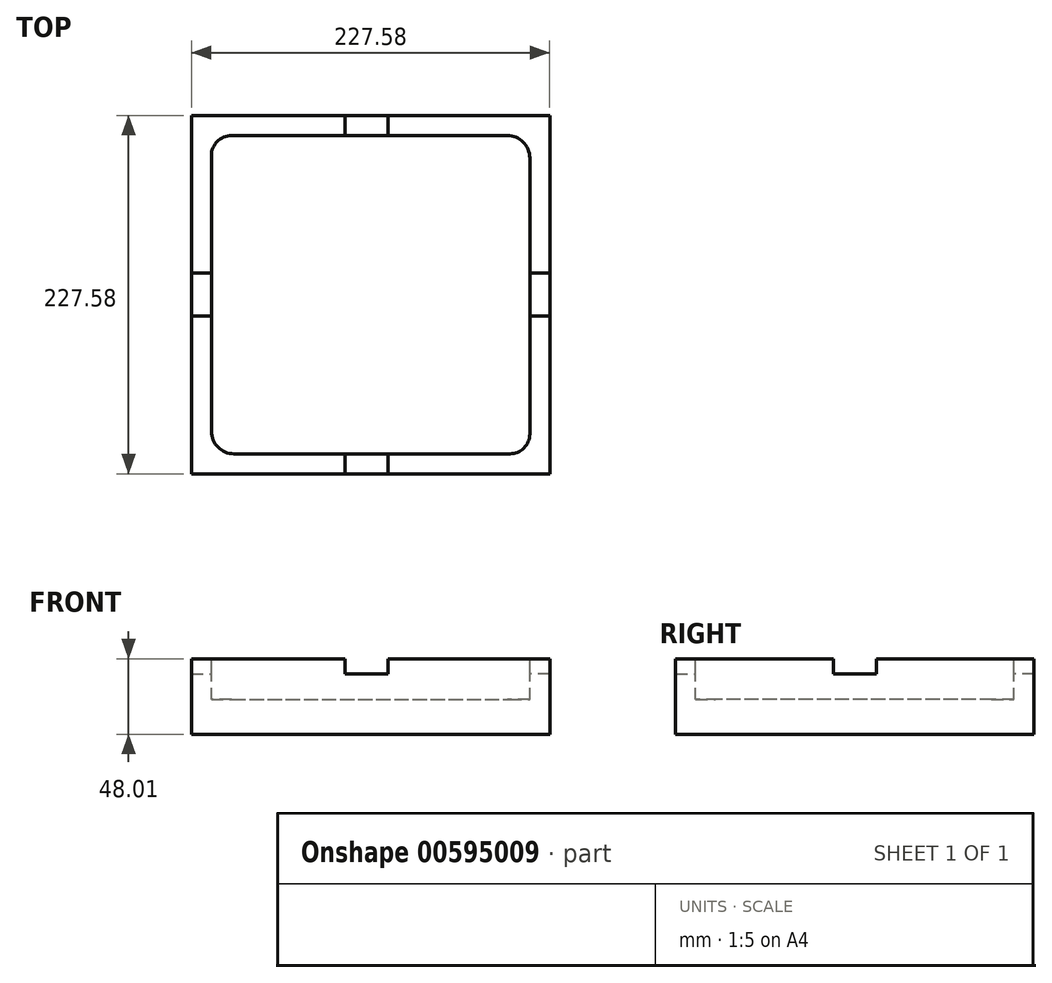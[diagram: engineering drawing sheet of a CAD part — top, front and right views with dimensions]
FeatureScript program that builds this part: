
annotation { "Feature Type Name" : "Feature", "Feature Type Description" : "" }
export const myFeature = defineFeature(function(context is Context, id is Id, definition is map)
    precondition{}
    {
        {
            var Q0;
            Q0=qCreatedBy(makeId("Top.planeOp"),FACE);
            var sketch = newSketch(context, id + "F0", { "sketchPlane" : qUnion([Q0])});
            skLineSegment(sketch, "E0.bottom", {"start": v(113.8, 113.8) * mm, "end": v(-113.8, 113.8) * mm});
            skLineSegment(sketch, "E0.top", {"start": v(113.8, -113.8) * mm, "end": v(-113.8, -113.8) * mm});
            skLineSegment(sketch, "E0.left", {"start": v(113.8, 113.8) * mm, "end": v(113.8, -113.8) * mm});
            skLineSegment(sketch, "E0.right", {"start": v(-113.8, 113.8) * mm, "end": v(-113.8, -113.8) * mm});
            skPoint(sketch, "E0.middle", {"position": v(0, 0) * mm});
            skLineSegment(sketch, "E1", {"start": v(0, -188.89) * mm, "end": v(0, 205.95) * mm, "construction": true});
            skPoint(sketch, "E1.startSnap0", {"position": v(0, -113.8) * mm});
            skPoint(sketch, "E1.endSnap0", {"position": v(0, 113.8) * mm});
            skLineSegment(sketch, "E2", {"start": v(-219.67, 0) * mm, "end": v(231.95, 0) * mm, "construction": true});
            skPoint(sketch, "E2.endSnap0", {"position": v(113.8, 0) * mm});
            skSolve(sketch);
        }
        {
            var Q0;
            Q0 = qSketchRegion(id + "F0", true);
            extrude(context, id + "F1", {"entities" : qUnion([Q0]), "depth" : 48 * mm, "offsetDistance" : 25.4 * mm});
        }
        {
            var Q0;
            Q0=makeQuery(id+"F1.opExtrude","CAP_FACE",FACE,{"disambiguationData":[OSD([sQuery(id+"F0.wireOp",EDGE,"E0.bottom"),sQuery(id+"F0.wireOp",EDGE,"E0.top"),sQuery(id+"F0.wireOp",EDGE,"E0.left"),sQuery(id+"F0.wireOp",EDGE,"E0.right")])],"isStart":false});
            var sketch = newSketch(context, id + "F2", { "sketchPlane" : qUnion([Q0])});
            skLineSegment(sketch, "E3", {"start": v(-88.4, 101.1) * mm, "end": v(86.8, 101.1) * mm});
            skLineSegment(sketch, "E4", {"start": v(-101.1, 88.4) * mm, "end": v(-101.1, -86.8) * mm});
            skLineSegment(sketch, "E5", {"start": v(0, -144.22) * mm, "end": v(0, 136.7) * mm, "construction": true});
            skLineSegment(sketch, "E6", {"start": v(188.13, 0) * mm, "end": v(-233, 0) * mm, "construction": true});
            skPoint(sketch, "E6.startSnap0", {"position": v(113.8, 0) * mm});
            skLineSegment(sketch, "E7.MirrorCS", {"start": v(-86.8, -101.1) * mm, "end": v(88.4, -101.1) * mm});
            skLineSegment(sketch, "E8.MirrorCS", {"start": v(101.1, 86.8) * mm, "end": v(101.1, -88.4) * mm});
            skArc(sketch, "E9.filletArc", {"start": v(-88.4, 101.1) * mm, "mid": v(-97.37, 97.37) * mm, "end": v(-101.1, 88.4) * mm});
            skPoint(sketch, "E10.visualSharp", {"position": v(101.1, -101.1) * mm});
            skArc(sketch, "E10.filletArc", {"start": v(88.4, -101.1) * mm, "mid": v(97.37, -97.37) * mm, "end": v(101.1, -88.4) * mm});
            skPoint(sketch, "E11.visualSharp", {"position": v(101.1, 101.1) * mm});
            skArc(sketch, "E11.filletArc", {"start": v(101.1, 86.8) * mm, "mid": v(96.9, 96.9) * mm, "end": v(86.8, 101.1) * mm});
            skPoint(sketch, "E12.visualSharp", {"position": v(-101.1, -101.1) * mm});
            skArc(sketch, "E12.filletArc", {"start": v(-101.1, -86.8) * mm, "mid": v(-96.9, -96.9) * mm, "end": v(-86.8, -101.1) * mm});
            skLineSegment(sketch, "E13", {"start": v(13.91, 101.1) * mm, "end": v(13.91, 113.8) * mm, "construction": true});
            skLineSegment(sketch, "E14", {"start": v(101.1, -11.17) * mm, "end": v(113.8, -11.17) * mm, "construction": true});
            skSolve(sketch);
        }
        {
            var Q0;
            Q0=makeQuery(id+"F2.imprint","IMPRINT",FACE,{"disambiguationData":[TD([[makeQuery(id+"F2.imprint","IMPRINT",EDGE,{"derivedFrom":sQuery(id+"F2.wireOp",EDGE,"E3")}),-1.0]])]});
            extrude(context, id + "F3", {"entities" : qUnion([Q0]), "operationType" : NewBodyOperationType.REMOVE, "oppositeDirection" : true, "depth" : 25.9 * mm, "offsetDistance" : 25.4 * mm});
        }
        {
            var Q0;
            Q0=makeQuery(id+"F1.opExtrude","CAP_FACE",FACE,{"disambiguationData":[OSD([sQuery(id+"F0.wireOp",EDGE,"E0.bottom"),sQuery(id+"F0.wireOp",EDGE,"E0.top"),sQuery(id+"F0.wireOp",EDGE,"E0.left"),sQuery(id+"F0.wireOp",EDGE,"E0.right")])],"isStart":false});
            var sketch = newSketch(context, id + "F4", { "sketchPlane" : qUnion([Q0])});
            skLineSegment(sketch, "E15", {"start": v(0, 153.68) * mm, "end": v(0, -179.49) * mm, "construction": true});
            skLineSegment(sketch, "E16", {"start": v(-246.34, 0) * mm, "end": v(288.7, 0) * mm, "construction": true});
            skLineSegment(sketch, "E17.bottom", {"start": v(11.1, 113.8) * mm, "end": v(-16.33, 113.8) * mm});
            skLineSegment(sketch, "E17.top", {"start": v(11.1, 101.1) * mm, "end": v(-16.33, 101.1) * mm});
            skLineSegment(sketch, "E17.left", {"start": v(11.1, 113.8) * mm, "end": v(11.1, 101.1) * mm});
            skLineSegment(sketch, "E17.right", {"start": v(-16.33, 113.8) * mm, "end": v(-16.33, 101.1) * mm});
            skPoint(sketch, "E17.middle", {"position": v(-2.61, 107.44) * mm});
            skLineSegment(sketch, "E18", {"start": v(113.8, 0) * mm, "end": v(101.1, 0) * mm});
            skLineSegment(sketch, "E19.bottom", {"start": v(113.8, 13.72) * mm, "end": v(101.1, 13.72) * mm});
            skLineSegment(sketch, "E19.top", {"start": v(113.8, -13.72) * mm, "end": v(101.1, -13.72) * mm});
            skLineSegment(sketch, "E19.left", {"start": v(113.8, 13.72) * mm, "end": v(113.8, -13.72) * mm});
            skLineSegment(sketch, "E19.right", {"start": v(101.1, 13.72) * mm, "end": v(101.1, -13.72) * mm});
            skPoint(sketch, "E19.middle", {"position": v(107.44, 0) * mm});
            skLineSegment(sketch, "E20.MirrorCS", {"start": v(11.1, -101.1) * mm, "end": v(-16.33, -101.1) * mm});
            skLineSegment(sketch, "E21.MirrorCS", {"start": v(11.1, -113.8) * mm, "end": v(-16.33, -113.8) * mm});
            skLineSegment(sketch, "E22.MirrorCS", {"start": v(11.1, -113.8) * mm, "end": v(11.1, -101.1) * mm});
            skLineSegment(sketch, "E23.MirrorCS", {"start": v(-16.33, -113.8) * mm, "end": v(-16.33, -101.1) * mm});
            skLineSegment(sketch, "E24.MirrorCS", {"start": v(-113.8, 13.72) * mm, "end": v(-101.1, 13.72) * mm});
            skLineSegment(sketch, "E25.MirrorCS", {"start": v(-101.1, 13.72) * mm, "end": v(-101.1, -13.72) * mm});
            skLineSegment(sketch, "E26.MirrorCS", {"start": v(-113.8, 13.72) * mm, "end": v(-113.8, -13.72) * mm});
            skLineSegment(sketch, "E27.MirrorCS", {"start": v(-113.8, -13.72) * mm, "end": v(-101.1, -13.72) * mm});
            skSolve(sketch);
        }
        {
            var Q0;
            Q0=makeQuery(id+"F4.imprint","IMPRINT",FACE,{"disambiguationData":[TD([[makeQuery(id+"F4.imprint","IMPRINT",EDGE,{"derivedFrom":sQuery(id+"F4.wireOp",EDGE,"E24.MirrorCS")}),-1.0]])]});
            var Q1;
            Q1=makeQuery(id+"F4.imprint","IMPRINT",FACE,{"disambiguationData":[TD([[makeQuery(id+"F4.imprint","IMPRINT",EDGE,{"derivedFrom":sQuery(id+"F4.wireOp",EDGE,"E17.bottom")}),1.0]])]});
            var Q2;
            {var subQ0=sQuery(id+"F4.wireOp",EDGE,"E18");Q2=makeQuery(id+"F4.imprint","IMPRINT",FACE,{"disambiguationData":[TD([[makeQuery(id+"F4.imprint","IMPRINT",EDGE,{"derivedFrom":subQ0}),-1.0]])]});}
            var Q3;
            {var subQ0=sQuery(id+"F4.wireOp",EDGE,"E18");Q3=makeQuery(id+"F4.imprint","IMPRINT",FACE,{"disambiguationData":[TD([[makeQuery(id+"F4.imprint","IMPRINT",EDGE,{"derivedFrom":subQ0}),1.0]])]});}
            var Q4;
            Q4=makeQuery(id+"F4.imprint","IMPRINT",FACE,{"disambiguationData":[TD([[makeQuery(id+"F4.imprint","IMPRINT",EDGE,{"derivedFrom":sQuery(id+"F4.wireOp",EDGE,"E20.MirrorCS")}),-1.0]])]});
            extrude(context, id + "F5", {"entities" : qUnion([Q0, Q1, Q2, Q3, Q4]), "operationType" : NewBodyOperationType.REMOVE, "oppositeDirection" : true, "depth" : 9.52 * mm, "offsetDistance" : 25.4 * mm});
        }
    });
